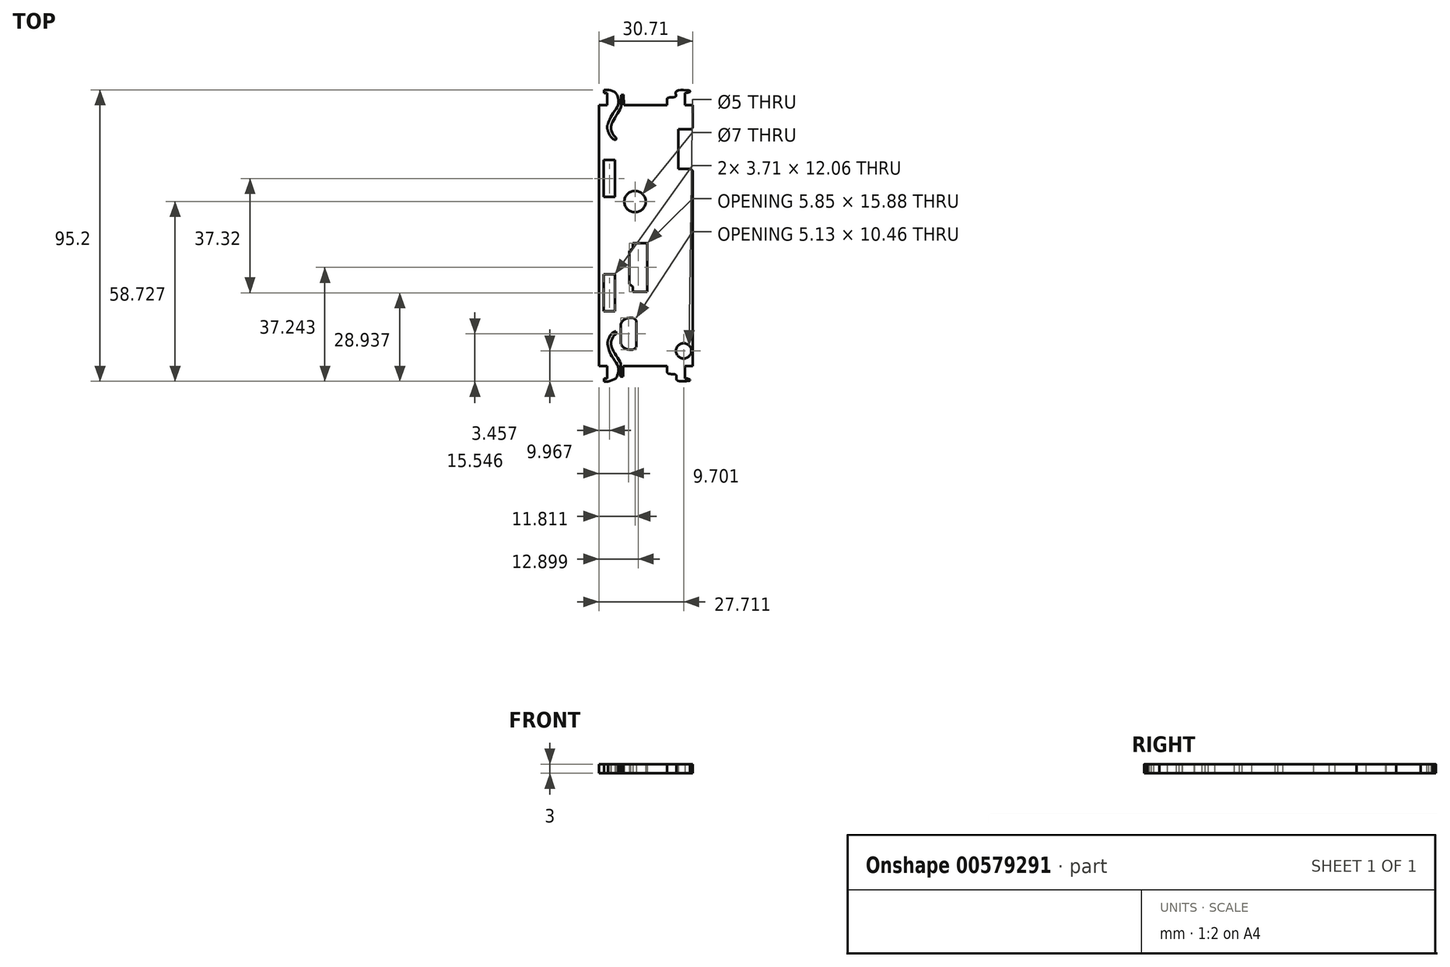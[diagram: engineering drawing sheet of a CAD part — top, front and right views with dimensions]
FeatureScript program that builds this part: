
annotation { "Feature Type Name" : "Feature", "Feature Type Description" : "" }
export const myFeature = defineFeature(function(context is Context, id is Id, definition is map)
    precondition{}
    {
        {
            var Q0;
            Q0=qCreatedBy(makeId("Top.planeOp"),FACE);
            var sketch = newSketch(context, id + "F0", { "sketchPlane" : qUnion([Q0])});
            skLineSegment(sketch, "E0.bottom", {"start": v(-33.02, 54.7) * mm, "end": v(-30.33, 54.7) * mm});
            skLineSegment(sketch, "E0.top", {"start": v(-33.02, -30.56) * mm, "end": v(-30.33, -30.56) * mm});
            skLineSegment(sketch, "E0.left", {"start": v(-33.02, 54.7) * mm, "end": v(-33.02, -30.56) * mm});
            skLineSegment(sketch, "E0.right", {"start": v(-2.3, 54.7) * mm, "end": v(-2.3, 47.77) * mm});
            skLineSegment(sketch, "E1.bottom", {"start": v(-31.42, 24.7) * mm, "end": v(-27.7, 24.7) * mm});
            skLineSegment(sketch, "E1.top", {"start": v(-31.42, 36.76) * mm, "end": v(-27.7, 36.76) * mm});
            skLineSegment(sketch, "E1.left", {"start": v(-31.42, 24.7) * mm, "end": v(-31.42, 36.76) * mm});
            skLineSegment(sketch, "E1.right", {"start": v(-27.7, 24.7) * mm, "end": v(-27.7, 36.76) * mm});
            skLineSegment(sketch, "E2.top", {"start": v(-31.33, 58.67) * mm, "end": v(-30.33, 58.67) * mm});
            skLineSegment(sketch, "E2.right", {"start": v(-30.33, 54.7) * mm, "end": v(-30.33, 58.67) * mm});
            skLineSegment(sketch, "E3", {"start": v(-31.33, 58.67) * mm, "end": v(-31.33, 59.67) * mm});
            skLineSegment(sketch, "E4", {"start": v(-31.33, 59.67) * mm, "end": v(-29.84, 59.67) * mm});
            skLineSegment(sketch, "E5", {"start": v(-30.33, 47.58) * mm, "end": v(-30.33, 47.36) * mm});
            skFitSpline(sketch, "E6", {"points": [v(-29.84, 59.67) * mm, v(-27.46, 58.61) * mm, v(-26.7, 56.68) * mm, v(-26.7, 54.7) * mm, v(-28.74, 51.54) * mm, v(-29.84, 49.1) * mm, v(-30.33, 47.58) * mm, v(-29.98, 46.14) * mm, v(-28.8, 44.06) * mm, v(-27.53, 43.4) * mm, v(-27.53, 43.73) * mm], "startDerivative": vector(24.68, -6.57) * mm, "endDerivative": vector(-9.27, 3.27) * mm});
            skFitSpline(sketch, "E7", {"points": [v(-27.53, 43.4) * mm, v(-27.32, 43.63) * mm, v(-27.48, 44.23) * mm, v(-28.14, 44.81) * mm, v(-28.95, 46.4) * mm, v(-29.02, 47.53) * mm, v(-28.74, 48.73) * mm, v(-27.4, 51.2) * mm, v(-25.9, 53.78) * mm, v(-25.68, 54.7) * mm], "startDerivative": vector(4.94, 3.3) * mm, "endDerivative": vector(1.2, 8.54) * mm});
            skLineSegment(sketch, "E8.trimOffspring", {"start": v(-24.87, 54.7) * mm, "end": v(-10.7, 54.7) * mm});
            skPoint(sketch, "E9.orphan", {"position": v(-30.33, 43.4) * mm});
            skPoint(sketch, "E10.trimOffspring.end.orphan", {"position": v(-24.74, 43.4) * mm});
            skLineSegment(sketch, "E11", {"start": v(-25.68, 54.7) * mm, "end": v(-25.72, 58.06) * mm});
            skLineSegment(sketch, "E12", {"start": v(-25.72, 58.06) * mm, "end": v(-24.91, 58.07) * mm});
            skLineSegment(sketch, "E13", {"start": v(-24.91, 58.07) * mm, "end": v(-24.87, 54.7) * mm});
            skPoint(sketch, "E14.start.orphan", {"position": v(-30.33, 56.68) * mm});
            skPoint(sketch, "E15.end.orphan", {"position": v(-24.91, 56.68) * mm});
            skLineSegment(sketch, "E16.right", {"start": v(-4.85, 54.7) * mm, "end": v(-4.85, 58.66) * mm});
            skLineSegment(sketch, "E17.top", {"start": v(-9.01, 57.25) * mm, "end": v(-9.01, 57.25) * mm});
            skLineSegment(sketch, "E17.left", {"start": v(-10.7, 54.7) * mm, "end": v(-10.7, 56.63) * mm});
            skFitSpline(sketch, "E18", {"points": [v(-4.85, 58.66) * mm, v(-3.87, 58.8) * mm, v(-3.27, 59.08) * mm, v(-3.23, 59.3) * mm, v(-3.8, 59.49) * mm, v(-7.17, 59.45) * mm, v(-7.95, 58.66) * mm, v(-7.84, 57.57) * mm, v(-9.01, 57.25) * mm, v(-10.3, 57.13) * mm, v(-10.7, 56.63) * mm], "startDerivative": vector(8.69, 1.47) * mm, "endDerivative": vector(-0.61, -8.23) * mm});
            skPoint(sketch, "E17.right.end.orphan", {"position": v(-7.33, 57.25) * mm});
            skLineSegment(sketch, "E19.trimOffspring", {"start": v(-4.85, 54.7) * mm, "end": v(-2.3, 54.7) * mm});
            skPoint(sketch, "E20.orphan", {"position": v(-10.7, 57.25) * mm});
            skLineSegment(sketch, "E21.MirrorCS", {"start": v(-31.33, -35.53) * mm, "end": v(-30.05, -35.53) * mm});
            skLineSegment(sketch, "E22.MirrorCS", {"start": v(-31.33, -34.53) * mm, "end": v(-30.33, -34.53) * mm});
            skLineSegment(sketch, "E23.MirrorCS", {"start": v(-31.33, -34.53) * mm, "end": v(-31.33, -35.53) * mm});
            skLineSegment(sketch, "E24.MirrorCS", {"start": v(-25.92, -33.93) * mm, "end": v(-25.12, -33.94) * mm});
            skLineSegment(sketch, "E25.MirrorCS", {"start": v(-9.8, -33.12) * mm, "end": v(-9.01, -33.12) * mm});
            skLineSegment(sketch, "E26.MirrorCS", {"start": v(-4.85, -30.56) * mm, "end": v(-2.3, -30.56) * mm});
            skLineSegment(sketch, "E27.MirrorCS", {"start": v(-30.33, -30.56) * mm, "end": v(-30.33, -34.53) * mm});
            skLineSegment(sketch, "E28.MirrorCS", {"start": v(-30.12, -23.45) * mm, "end": v(-30.12, -22.75) * mm});
            skLineSegment(sketch, "E29.MirrorCS", {"start": v(-10.7, -30.56) * mm, "end": v(-10.7, -32.5) * mm});
            skFitSpline(sketch, "E30.MirrorCS", {"points": [v(-27.53, -19.26) * mm, v(-27.32, -19.5) * mm, v(-27.48, -20.1) * mm, v(-28.14, -20.68) * mm, v(-28.95, -22.27) * mm, v(-29.02, -23.4) * mm, v(-28.74, -24.6) * mm, v(-27.4, -27.06) * mm, v(-25.9, -29.64) * mm, v(-25.88, -30.56) * mm], "startDerivative": vector(4.94, -3.3) * mm, "endDerivative": vector(1.2, -8.54) * mm});
            skPoint(sketch, "E31.MirrorP", {"position": v(-30.12, -32.55) * mm});
            skLineSegment(sketch, "E32.MirrorCS", {"start": v(-25.12, -33.94) * mm, "end": v(-25.08, -30.56) * mm});
            skLineSegment(sketch, "E33.MirrorCS", {"start": v(-25.88, -30.56) * mm, "end": v(-25.92, -33.93) * mm});
            skLineSegment(sketch, "E34.MirrorCS", {"start": v(-31.42, -12.62) * mm, "end": v(-27.7, -12.62) * mm});
            skFitSpline(sketch, "E35.MirrorCS", {"points": [v(-4.85, -34.53) * mm, v(-3.87, -34.67) * mm, v(-3.27, -34.94) * mm, v(-3.23, -35.16) * mm, v(-3.8, -35.35) * mm, v(-7.17, -35.32) * mm, v(-7.75, -34.53) * mm, v(-7.84, -33.44) * mm, v(-9.01, -33.12) * mm, v(-10.3, -33) * mm, v(-10.7, -32.5) * mm], "startDerivative": vector(8.69, -1.47) * mm, "endDerivative": vector(-0.61, 8.23) * mm});
            skPoint(sketch, "E36.MirrorP", {"position": v(-10.48, -33.12) * mm});
            skPoint(sketch, "E37.MirrorP", {"position": v(-30.12, -19.26) * mm});
            skLineSegment(sketch, "E38.MirrorCS", {"start": v(-31.42, -0.56) * mm, "end": v(-31.42, -12.62) * mm});
            skPoint(sketch, "E39.MirrorP", {"position": v(-7.54, -33.12) * mm});
            skLineSegment(sketch, "E40.MirrorCS", {"start": v(-27.7, -0.56) * mm, "end": v(-27.7, -12.62) * mm});
            skFitSpline(sketch, "E41.MirrorCS", {"points": [v(-30.05, -35.53) * mm, v(-27.46, -34.48) * mm, v(-26.7, -32.55) * mm, v(-26.7, -30.56) * mm, v(-28.74, -27.4) * mm, v(-29.84, -24.96) * mm, v(-30.12, -23.45) * mm, v(-29.98, -22) * mm, v(-28.8, -19.93) * mm, v(-27.53, -19.26) * mm, v(-27.53, -19.6) * mm], "startDerivative": vector(24.68, 6.57) * mm, "endDerivative": vector(-9.27, -3.27) * mm});
            skLineSegment(sketch, "E42.MirrorCS", {"start": v(-25.08, -30.56) * mm, "end": v(-10.7, -30.56) * mm});
            skPoint(sketch, "E43.MirrorP", {"position": v(-24.91, -32.55) * mm});
            skLineSegment(sketch, "E44.MirrorCS", {"start": v(-31.42, -0.56) * mm, "end": v(-27.7, -0.56) * mm});
            skLineSegment(sketch, "E45.MirrorCS", {"start": v(-4.85, -30.56) * mm, "end": v(-4.85, -34.53) * mm});
            skPoint(sketch, "E46.end.orphan", {"position": v(-33.02, 12.07) * mm});
            skPoint(sketch, "E46.start.orphan", {"position": v(-2.3, 12.07) * mm});
            skLineSegment(sketch, "E47.bottom", {"start": v(-7.03, 33.82) * mm, "end": v(-3.3, 33.82) * mm});
            skLineSegment(sketch, "E47.top", {"start": v(-7.03, 46.77) * mm, "end": v(-3.3, 46.77) * mm});
            skLineSegment(sketch, "E47.left", {"start": v(-7.03, 33.82) * mm, "end": v(-7.03, 46.77) * mm});
            skLineSegment(sketch, "E48", {"start": v(-2.3, 46.77) * mm, "end": v(-3.3, 46.77) * mm});
            skArc(sketch, "E49", {"start": v(-2.3, 32.82) * mm, "mid": v(-2.6, 33.53) * mm, "end": v(-3.3, 33.82) * mm});
            skArc(sketch, "E50", {"start": v(-3.3, 46.77) * mm, "mid": v(-2.6, 47.07) * mm, "end": v(-2.3, 47.77) * mm});
            skLineSegment(sketch, "E51.trimOffspring", {"start": v(-2.3, 32.82) * mm, "end": v(-2.3, -30.56) * mm});
            skPoint(sketch, "E52.orphan", {"position": v(-2.3, 33.82) * mm});
            skCircle(sketch, "E53", {"center": v(-5.3, -25.56) * mm, "radius": 2.5 * mm});
            skCircle(sketch, "E54", {"center": v(-21.2, 23.2) * mm, "radius": 3.5 * mm});
            skLineSegment(sketch, "E55.bottom", {"start": v(-21.9, -6.23) * mm, "end": v(-17.2, -6.23) * mm});
            skLineSegment(sketch, "E55.top", {"start": v(-21.9, 9.65) * mm, "end": v(-17.2, 9.65) * mm});
            skLineSegment(sketch, "E55.left", {"start": v(-23.05, -3.68) * mm, "end": v(-23.05, 7.1) * mm});
            skLineSegment(sketch, "E55.right", {"start": v(-17.2, -6.23) * mm, "end": v(-17.2, 9.65) * mm});
            skLineSegment(sketch, "E56", {"start": v(-21.9, 9.65) * mm, "end": v(-21.9, 8) * mm});
            skLineSegment(sketch, "E57", {"start": v(-21.9, 8) * mm, "end": v(-23.05, 7.1) * mm});
            skLineSegment(sketch, "E58.MirrorCS", {"start": v(-23.05, 7.1) * mm, "end": v(-23.05, -3.68) * mm});
            skLineSegment(sketch, "E59.MirrorCS", {"start": v(-21.9, -6.23) * mm, "end": v(-21.9, -4.57) * mm});
            skLineSegment(sketch, "E60.MirrorCS", {"start": v(-21.9, -4.57) * mm, "end": v(-23.05, -3.68) * mm});
            skPoint(sketch, "E61.orphan", {"position": v(-23.05, -6.23) * mm});
            skPoint(sketch, "E62.MirrorCS.end.orphan", {"position": v(-17.2, -6.23) * mm});
            skPoint(sketch, "E63.orphan", {"position": v(-23.05, 9.65) * mm});
            skPoint(sketch, "E64.end.orphan", {"position": v(-23.05, 1.71) * mm});
            skPoint(sketch, "E64.start.orphan", {"position": v(-17.2, 1.71) * mm});
            skPoint(sketch, "E65.MirrorP", {"position": v(-25.28, -21.44) * mm});
            skLineSegment(sketch, "E66.bottom", {"start": v(-22.9, -25.22) * mm, "end": v(-22.37, -25.22) * mm});
            skLineSegment(sketch, "E66.top", {"start": v(-22.9, -14.75) * mm, "end": v(-22.37, -14.75) * mm});
            skLineSegment(sketch, "E66.left", {"start": v(-25.88, -23.21) * mm, "end": v(-25.88, -16.76) * mm});
            skLineSegment(sketch, "E66.right", {"start": v(-20.75, -24.22) * mm, "end": v(-20.75, -15.75) * mm});
            skArc(sketch, "E67", {"start": v(-20.75, -15.75) * mm, "mid": v(-21.56, -14.98) * mm, "end": v(-22.65, -14.75) * mm});
            skArc(sketch, "E68.MirrorCS", {"start": v(-20.75, -24.22) * mm, "mid": v(-21.56, -24.99) * mm, "end": v(-22.65, -25.22) * mm});
            skPoint(sketch, "E69.orphan", {"position": v(-25.88, -25.22) * mm});
            skPoint(sketch, "E70.orphan", {"position": v(-20.75, -25.22) * mm});
            skPoint(sketch, "E71.orphan", {"position": v(-20.75, -14.75) * mm});
            skPoint(sketch, "E72.orphan", {"position": v(-25.88, -14.75) * mm});
            skArc(sketch, "E73", {"start": v(-22.65, -14.75) * mm, "mid": v(-24.57, -15.26) * mm, "end": v(-25.88, -16.76) * mm});
            skArc(sketch, "E74.MirrorCS", {"start": v(-22.65, -25.22) * mm, "mid": v(-24.57, -24.7) * mm, "end": v(-25.88, -23.21) * mm});
            skPoint(sketch, "E75.start.orphan", {"position": v(-24.82, -14.75) * mm});
            skPoint(sketch, "E76.orphan", {"position": v(-24.82, -25.22) * mm});
            skPoint(sketch, "E77.end.orphan", {"position": v(-25.88, -19.98) * mm});
            skPoint(sketch, "E77.start.orphan", {"position": v(-20.75, -19.98) * mm});
            skSolve(sketch);
        }
        {
            var Q0;
            Q0=makeQuery(id+"F0.imprint","IMPRINT",FACE,{"disambiguationData":[TD([[makeQuery(id+"F0.imprint","IMPRINT",EDGE,{"derivedFrom":sQuery(id+"F0.wireOp",EDGE,"E0.left")}),1.0]])]});
            extrude(context, id + "F1", {"entities" : qUnion([Q0]), "depth" : 3 * mm, "offsetDistance" : 25.4 * mm});
        }
    });
